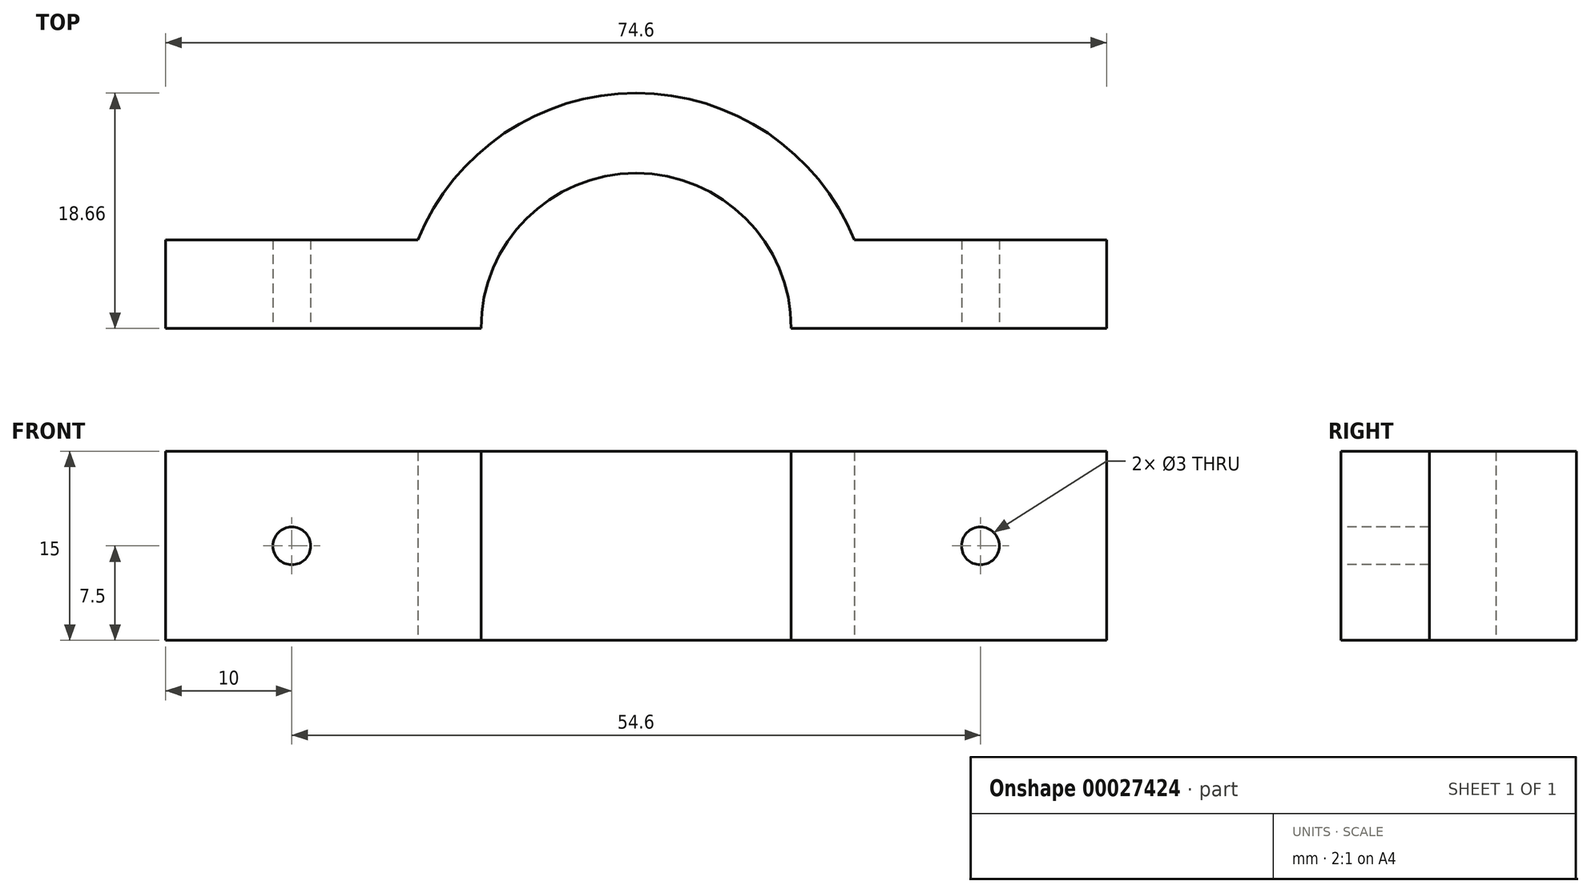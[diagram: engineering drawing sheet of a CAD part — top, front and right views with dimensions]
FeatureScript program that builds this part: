
annotation { "Feature Type Name" : "Feature", "Feature Type Description" : "" }
export const myFeature = defineFeature(function(context is Context, id is Id, definition is map)
    precondition{}
    {
        {
            var Q0;
            Q0=qCreatedBy(makeId("Top.planeOp"),FACE);
            var sketch = newSketch(context, id + "F0", { "sketchPlane" : qUnion([Q0])});
            skArc(sketch, "E0", {"start": v(12.3, 0) * mm, "mid": v(0, 12.3) * mm, "end": v(-12.3, 0) * mm});
            skArc(sketch, "E1", {"start": v(17.3, 7) * mm, "mid": v(0, 18.66) * mm, "end": v(-17.3, 7) * mm});
            skLineSegment(sketch, "E2.rect.top", {"start": v(37.3, 7) * mm, "end": v(17.3, 7) * mm});
            skLineSegment(sketch, "E2.rect.left", {"start": v(37.3, 0) * mm, "end": v(37.3, 7) * mm});
            skLineSegment(sketch, "E2.rect.right", {"start": v(-37.3, 0) * mm, "end": v(-37.3, 7) * mm});
            skLineSegment(sketch, "E3", {"start": v(-37.3, 0) * mm, "end": v(-12.3, 0) * mm});
            skPoint(sketch, "E4.trimOffspring.end.orphan", {"position": v(-37.3, -7) * mm});
            skPoint(sketch, "E5.orphan", {"position": v(37.3, -7) * mm});
            skLineSegment(sketch, "E6.trimOffspring", {"start": v(12.3, 0) * mm, "end": v(37.3, 0) * mm});
            skLineSegment(sketch, "E7.trimOffspring", {"start": v(-17.3, 7) * mm, "end": v(-37.3, 7) * mm});
            skSolve(sketch);
        }
        {
            var Q0;
            Q0=makeQuery(id+"F0.imprint","IMPRINT",FACE,{"disambiguationData":[TD([[makeQuery(id+"F0.imprint","IMPRINT",EDGE,{"derivedFrom":sQuery(id+"F0.wireOp",EDGE,"E0")}),-1.0]])]});
            extrude(context, id + "F1", {"entities" : qUnion([Q0]), "depth" : 15 * mm});
        }
        {
            var Q0;
            Q0=makeQuery(id+"F1.opExtrude","SWEPT_FACE",FACE,{"disambiguationData":[OSD([sQuery(id+"F0.wireOp",EDGE,"E3")])]});
            var sketch = newSketch(context, id + "F2", { "sketchPlane" : qUnion([Q0])});
            skCircle(sketch, "E8", {"center": v(-27.3, 7.5) * mm, "radius": 1.5 * mm});
            skCircle(sketch, "E9", {"center": v(27.3, 7.5) * mm, "radius": 1.5 * mm});
            skSolve(sketch);
        }
        {
            var Q0;
            Q0=makeQuery(id+"F2.imprint","IMPRINT",FACE,{"disambiguationData":[TD([[makeQuery(id+"F2.imprint","IMPRINT",EDGE,{"derivedFrom":sQuery(id+"F2.wireOp",EDGE,"E8")}),1.0]])]});
            var Q1;
            Q1=makeQuery(id+"F2.imprint","IMPRINT",FACE,{"disambiguationData":[TD([[makeQuery(id+"F2.imprint","IMPRINT",EDGE,{"derivedFrom":sQuery(id+"F2.wireOp",EDGE,"E9")}),1.0]])]});
            extrude(context, id + "F3", {"entities" : qUnion([Q0, Q1]), "operationType" : NewBodyOperationType.REMOVE, "oppositeDirection" : true, "depth" : 7.5 * mm});
        }
    });
